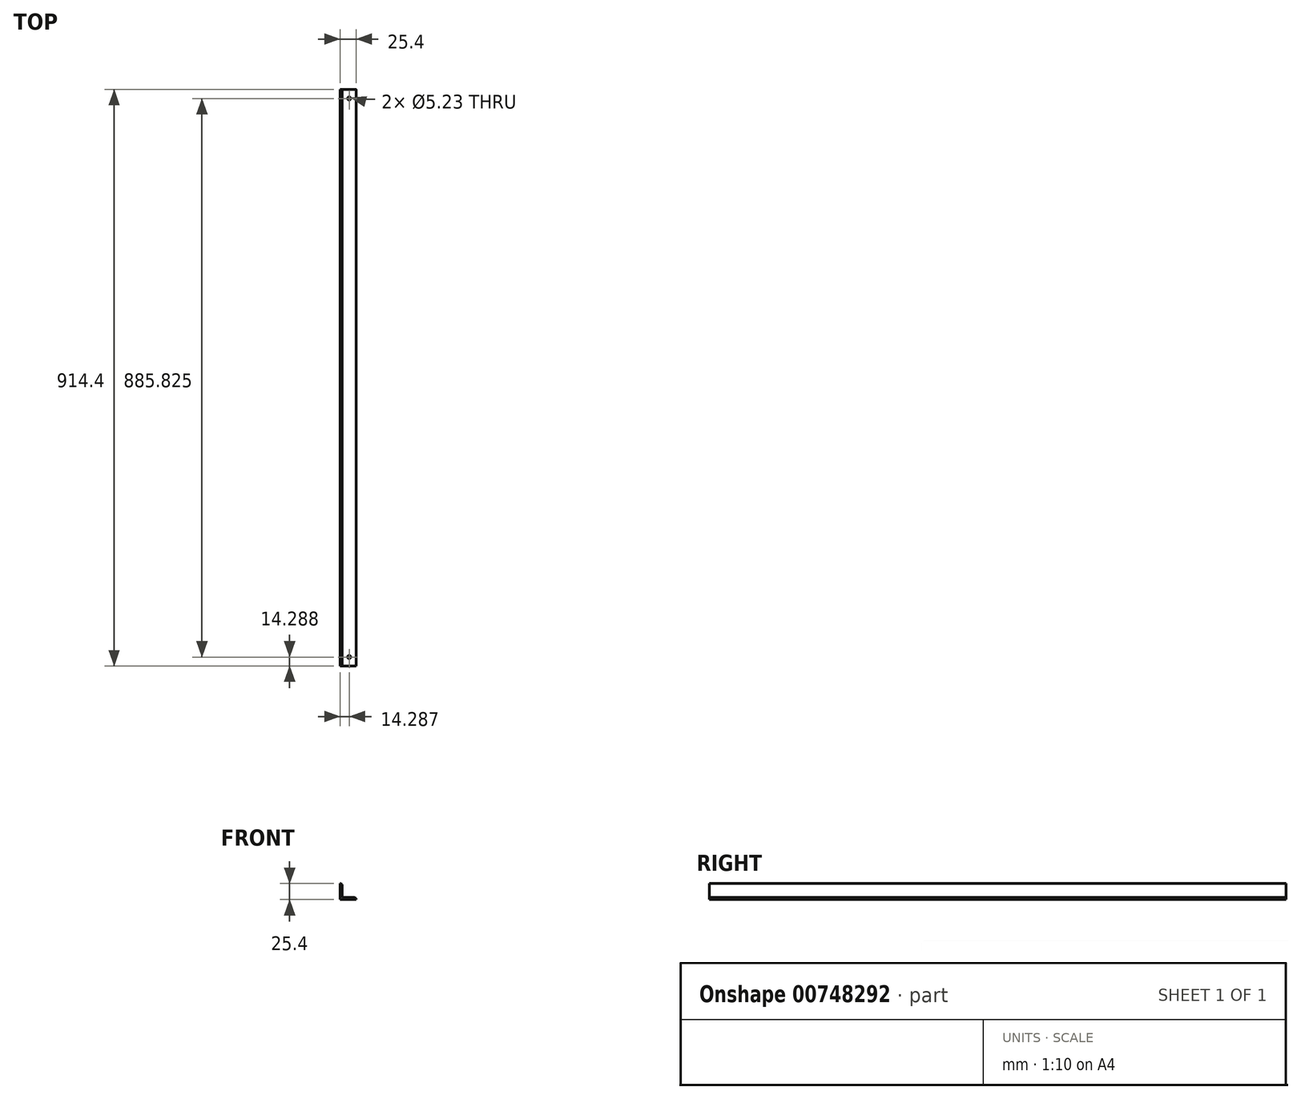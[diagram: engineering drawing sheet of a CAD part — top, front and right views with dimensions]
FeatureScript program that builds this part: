
annotation { "Feature Type Name" : "Feature", "Feature Type Description" : "" }
export const myFeature = defineFeature(function(context is Context, id is Id, definition is map)
    precondition{}
    {
        {
            var Q0;
            Q0=qCreatedBy(makeId("Front.planeOp"),FACE);
            var sketch = newSketch(context, id + "F0", { "sketchPlane" : qUnion([Q0])});
            skLineSegment(sketch, "E0", {"start": v(0, 0) * mm, "end": v(-25.4, 0) * mm});
            skLineSegment(sketch, "E1", {"start": v(-25.4, 0) * mm, "end": v(-25.4, 25.4) * mm});
            skLineSegment(sketch, "E2", {"start": v(-25.4, 25.4) * mm, "end": v(-25.4, 25.4) * mm});
            skLineSegment(sketch, "E3", {"start": v(-22.23, 22.23) * mm, "end": v(-22.23, 6.35) * mm});
            skLineSegment(sketch, "E4", {"start": v(-19.05, 3.18) * mm, "end": v(-3.18, 3.18) * mm});
            skLineSegment(sketch, "E5", {"start": v(0, 0) * mm, "end": v(0, 0) * mm});
            skPoint(sketch, "E6.visualSharp", {"position": v(-22.23, 3.18) * mm});
            skArc(sketch, "E6.filletArc", {"start": v(-22.23, 6.35) * mm, "mid": v(-21.3, 4.1) * mm, "end": v(-19.05, 3.18) * mm});
            skPoint(sketch, "E7.visualSharp", {"position": v(-22.23, 25.4) * mm});
            skArc(sketch, "E7.filletArc", {"start": v(-22.23, 22.23) * mm, "mid": v(-23.15, 24.47) * mm, "end": v(-25.4, 25.4) * mm});
            skPoint(sketch, "E8.visualSharp", {"position": v(0, 3.18) * mm});
            skArc(sketch, "E8.filletArc", {"start": v(0, 0) * mm, "mid": v(-0.93, 2.25) * mm, "end": v(-3.18, 3.18) * mm});
            skSolve(sketch);
        }
        {
            var Q0;
            Q0=qSketchRegion(id+"F0",true);
            extrude(context, id + "F1", {"entities" : qUnion([Q0]), "depth" : 914.4 * mm, "offsetDistance" : 25.4 * mm});
        }
        {
            var Q0;
            Q0=makeQuery(id+"F1.opExtrude","SWEPT_FACE",FACE,{"disambiguationData":[OSD([sQuery(id+"F0.wireOp",EDGE,"E4")])]});
            var sketch = newSketch(context, id + "F2", { "sketchPlane" : qUnion([Q0])});
            skLineSegment(sketch, "E9", {"start": v(-11.11, -914.4) * mm, "end": v(-11.11, 0) * mm, "construction": true});
            skLineSegment(sketch, "E10", {"start": v(-3.18, -900.11) * mm, "end": v(-19.05, -900.11) * mm, "construction": true});
            skCircle(sketch, "E11", {"center": v(-11.11, -900.11) * mm, "radius": 2.62 * mm});
            skLineSegment(sketch, "E12", {"start": v(-19.05, -14.29) * mm, "end": v(-3.18, -14.29) * mm, "construction": true});
            skCircle(sketch, "E13", {"center": v(-11.11, -14.29) * mm, "radius": 2.62 * mm});
            skSolve(sketch);
        }
        {
            var Q0;
            Q0=qSketchRegion(id+"F2",true);
            extrude(context, id + "F3", {"entities" : qUnion([Q0]), "operationType" : NewBodyOperationType.REMOVE, "endBound" : BoundingType.THROUGH_ALL, "oppositeDirection" : true, "depth" : 25.4 * mm, "offsetDistance" : 25.4 * mm});
        }
    });
